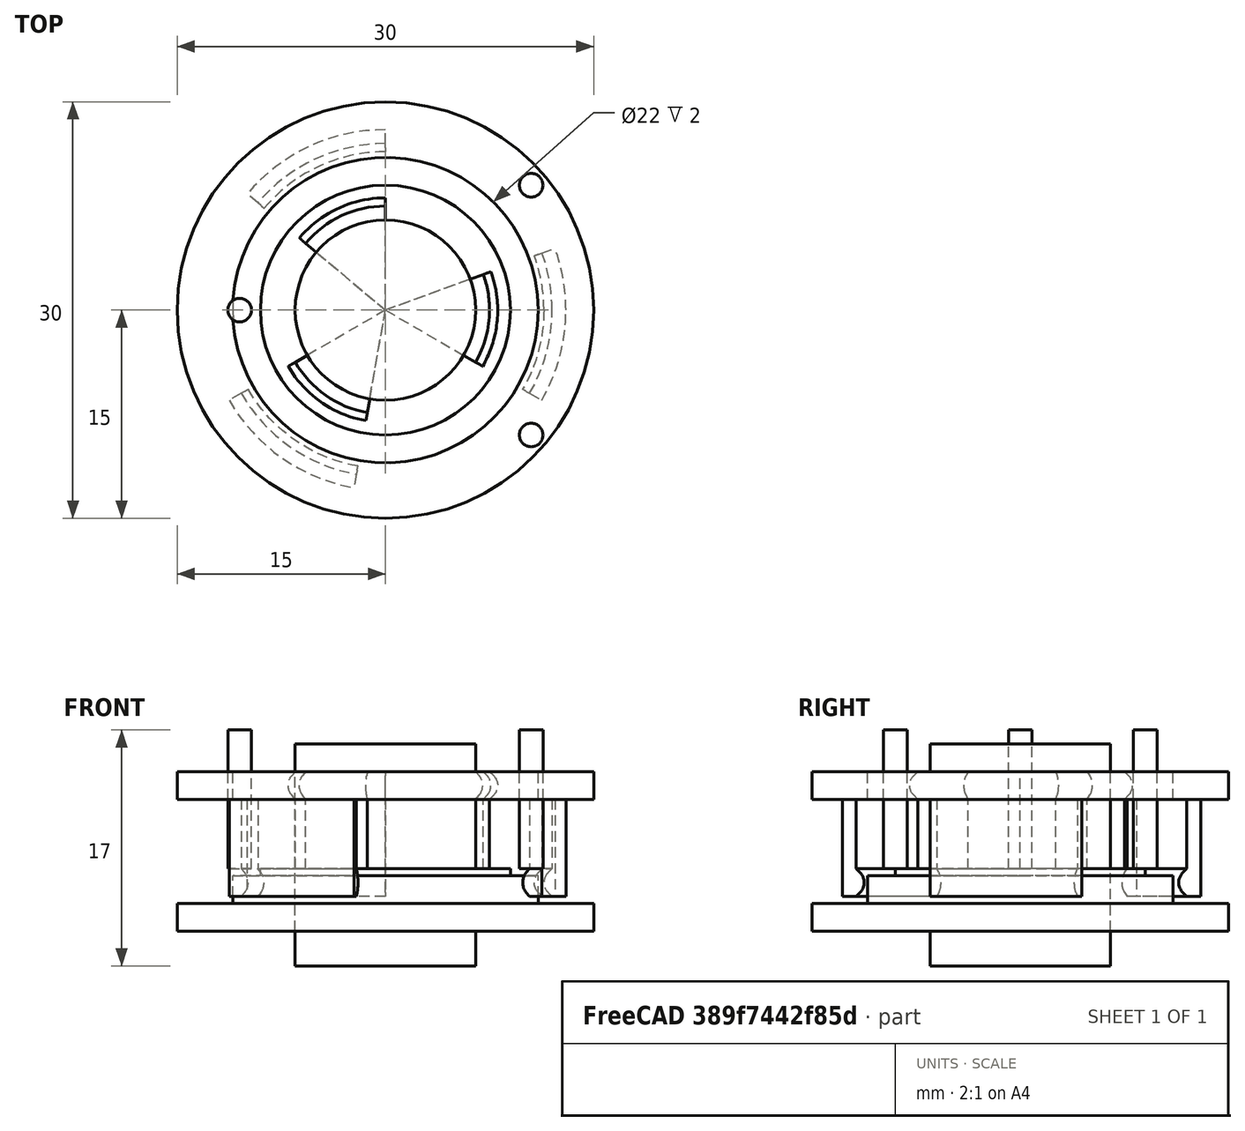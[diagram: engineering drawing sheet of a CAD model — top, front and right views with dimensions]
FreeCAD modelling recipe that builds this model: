
FCSTD DOCUMENT  (FreeCAD 0.16R6703 (Git))
Label: bearing-test-2
License: All rights reserved
LicenseURL: http://en.wikipedia.org/wiki/All_rights_reserved
objects: Part::Cylinder×12, Part::MultiFuse×6, Part::Cut×5, Part::Cone×4, Part::Box×4, Part::Feature×4, Part::Mirroring×3, Part::Fillet×2, Part::MultiCommon×2, App::DocumentObjectGroup×1
note: 42 computed .brp shape members not serialized (recipe doc carries the construction recipe); baked Part::Feature solids carry a one-line shape summary decoded from their .brp

FEATURE [Part::Cylinder] Cylinder
  Angle = 360
  Height = 5
  Radius = 7.5
FEATURE [Part::Cylinder] Cylinder001
  Angle = 360
  Height = 6
  Placement = pos=(0,0,-1) rot=(0,0,1;0rad)
  Radius = 12
FEATURE [Part::Cylinder] Cylinder002
  Angle = 360
  Height = 16
  Placement = pos=(0,0,-7) rot=(0,0,1;0rad)
  Radius = 6.5
FEATURE [Part::Cone] Cone
  Angle = 360
  Height = 1
  Placement = pos=(0,0,5) rot=(0,0,1;0rad)
  Radius1 = 7.5
  Radius2 = 8.5
FEATURE [Part::Cone] Cone001
  Angle = 360
  Height = 1
  Placement = pos=(0,0,5) rot=(0,0,1;0rad)
  Radius1 = 7.5
  Radius2 = 8.5
FEATURE [Part::Mirroring] Part__Mirroring  label="Cone001 (Mirror #1)"
  Base = (0,0,6)
  Normal = (0,0,1)
  Source = -> Cone001
FEATURE [Part::MultiFuse] Fusion
  Shapes = -> [Cylinder,Cone,Part__Mirroring]
FEATURE [Part::Fillet] Fillet
  Base = -> Fusion
  Edges = 1 edges r=1: [Edge3]
FEATURE [Part::Box] Box  label="Cube"
  Height = 10
  Length = 10
  Placement = pos=(0,0,-1) rot=(0,0,1;0rad)
  Width = 10
FEATURE [Part::Box] Box001  label="Cube001"
  Height = 10
  Length = 10
  Placement = pos=(0,0,-1) rot=(0,0,1;0.349066rad)
  Width = 10
FEATURE [Part::MultiCommon] Common
  Shapes = -> [Box,Box001]
FEATURE [Part::Feature] Common001
  Placement = pos=(0,0,0) rot=(0,0,1;2.0944rad)
  shape: bbox 12.16 x 11.43 x 10 mm, 6 faces (baked)
FEATURE [Part::Feature] Common002
  Placement = pos=(0,0,0) rot=(0,0,1;4.18879rad)
  shape: bbox 10.4 x 11.06 x 10 mm, 6 faces (baked)
FEATURE [Part::MultiFuse] Fusion001
  Shapes = -> [Common,Common001,Common002]
FEATURE [Part::Cut] Cut
  Base = -> Fillet
  Tool = -> Fusion001
FEATURE [Part::Cylinder] Cylinder003
  Angle = 360
  Height = 0.5
  Placement = pos=(0,0,-0.5) rot=(0,0,1;0rad)
  Radius = 9
FEATURE [Part::Cylinder] Cylinder004
  Angle = 360
  Height = 2
  Placement = pos=(0,0,-2.5) rot=(0,0,1;0rad)
  Radius = 11
FEATURE [Part::Cylinder] Cylinder005
  Angle = 360
  Height = 7
  Radius = 13
FEATURE [Part::Cone] Cone002
  Angle = 360
  Height = 1
  Placement = pos=(0,0,5) rot=(0,0,1;0rad)
  Radius1 = 12
  Radius2 = 11
FEATURE [Part::Cone] Cone003
  Angle = 360
  Height = 1
  Placement = pos=(0,0,5) rot=(0,0,1;0rad)
  Radius1 = 12
  Radius2 = 11
FEATURE [Part::Mirroring] Part__Mirroring001  label="Cone003 (Mirror #2)"
  Base = (0,0,6)
  Normal = (0,0,1)
  Source = -> Cone003
FEATURE [Part::MultiFuse] Fusion004
  Shapes = -> [Cone002,Part__Mirroring001]
FEATURE [Part::Fillet] Fillet001
  Base = -> Fusion004
  Edges = 1 edges r=1: [Edge3]
FEATURE [Part::Cut] Cut002
  Base = -> Cylinder005
  Tool = -> Fillet001
FEATURE [Part::Cut] Cut003
  Base = -> Cut002
  Tool = -> Cylinder001
FEATURE [Part::Box] Box002  label="Cube002"
  Height = 10
  Length = 16
  Width = 16
FEATURE [Part::Box] Box003  label="Cube003"
  Height = 10
  Length = 16
  Placement = pos=(0,0,0) rot=(0,0,1;0.349066rad)
  Width = 16
FEATURE [Part::MultiCommon] Common003
  Shapes = -> [Box002,Box003]
FEATURE [Part::Feature] Common003001
  Placement = pos=(0,0,0) rot=(0,0,1;2.0944rad)
  shape: bbox 19.46 x 18.28 x 10 mm, 6 faces (baked)
FEATURE [Part::Feature] Common003002
  Placement = pos=(0,0,0) rot=(0,0,1;4.18879rad)
  shape: bbox 16.63 x 17.7 x 10 mm, 6 faces (baked)
FEATURE [Part::MultiFuse] Fusion005
  Shapes = -> [Common003,Common003001,Common003002]
FEATURE [Part::Cut] Cut004
  Base = -> Cut003
  Tool = -> Fusion005
FEATURE [Part::Mirroring] Part__Mirroring002  label="Cut004 (Mirror #3)"
  Base = (0,0,0)
  Normal = (0,0,1)
  Placement = pos=(0,0,5) rot=(0,0,1;0rad)
  Source = -> Cut004
FEATURE [Part::Cylinder] Cylinder006
  Angle = 360
  Height = 2
  Placement = pos=(0,0,5) rot=(0,0,1;0rad)
  Radius = 15
FEATURE [Part::MultiFuse] Fusion006
  Shapes = -> [Part__Mirroring002,Cylinder006]
FEATURE [Part::Cylinder] Cylinder007
  Angle = 360
  Height = 10
  Radius = 11
FEATURE [Part::Cut] Cut005
  Base = -> Fusion006
  Tool = -> Cylinder007
FEATURE [Part::Cylinder] Cylinder008
  Angle = 360
  Height = 2
  Placement = pos=(0,0,-4.5) rot=(0,0,1;0rad)
  Radius = 15
FEATURE [Part::Cylinder] Cylinder009
  Angle = 360
  Height = 10
  Placement = pos=(10.5,9,0) rot=(0,0,1;0rad)
  Radius = 0.85
FEATURE [Part::Cylinder] Cylinder010
  Angle = 360
  Height = 10
  Placement = pos=(10.5,-9,0) rot=(0,0,1;0rad)
  Radius = 0.85
FEATURE [Part::Cylinder] Cylinder011
  Angle = 360
  Height = 10
  Placement = pos=(-10.5,0,0) rot=(0,0,1;0rad)
  Radius = 0.85
FEATURE [Part::MultiFuse] Fusion007
  Shapes = -> [Cylinder003,Cut]
FEATURE [App::DocumentObjectGroup] Group  label="bearing"
  Group = -> [Cylinder002,Cylinder004,Cut005,Cylinder008,Fusion007]
